# Revit family: Hose_Box-Bradley_Corp-7904VB
name_source: partatom
category: Plumbing Fixtures
units: mm (PartAtom-declared; Revit-internal decimal feet)

## family parameters
Cut with Voids When Loaded = No
Host = Face
Part Type = Normal
Room Calculation Point = No
Round Connector Dimension = Use Radius
Shared = No

## types (1)
- 7904VB
    ADA Compliant = No
    Assembly Code = D2090800
    Box Depth = 2 "
    Box Height = 10 "
    Box Width = 8 "
    Buy American Act = To Be Determined
    CWFU = 0
    Cold Inlet Elevation = Elevation - 1.667
    Cold Water Connection Diameter = 1"
    Cold Water Connection Radius = 0"
    Default Elevation = 48 "
    Depth = 3.75 "
    Description = Hose Box – Recessed
    Door Width = 7.5 "
    Frame Width = 1.375 "
    HWFU = 0
    Height = 12.25 "
    Hose Box Material = Metal - Bradley Corp - Stainless Steel - Satin
    Hose Outlet Connection Diameter = 1"
    Hose Outlet Connection Radius = 0"
    Hot Inlet Elevation = Elevation + 1.667
    Hot Water Connection Diameter = 1"
    Hot Water Connection Radius = 0"
    Installation Type = Wall Mounted - Recessed
    Low Emitting Material = No
    Manufacturer = Bradley Corporation
    Manufacturer Installation URL - English = https://www.bradleycorp.com
    MasterFormat Number = 22 05 23
    MasterFormat Title = General-Duty Valves for Plumbing Piping
    Material = Cast Brass
    Model = 7904VB
    OmniClass Code = 23.27.31.29.11
    OmniClass Title = Manual Mixing Valves
    Percentage of Recycled Content = 0
    Product Page URL = https://www.bradleycorp.com
    Product Tech Data URL - English = https://www.bradleycorp.com
    Specifications URL = https://www.bradleycorp.com
    Type Comments = w/ Vacuum Breaker
    URL = http://www.bradleycorp.com
    Valve Material = Metal - Bradley Corp - Cast Brass
    Valve Material - Exposed = Metal - Bradley Corp - Chrome
    Vent Connection = No
    Version = 1.0
    Waste Connection = No
    Width = 10.25 "

## geometry (parser evidence)
native form markers: Blend x2, Sweep x5
no freeform markers — native parametric forms only
